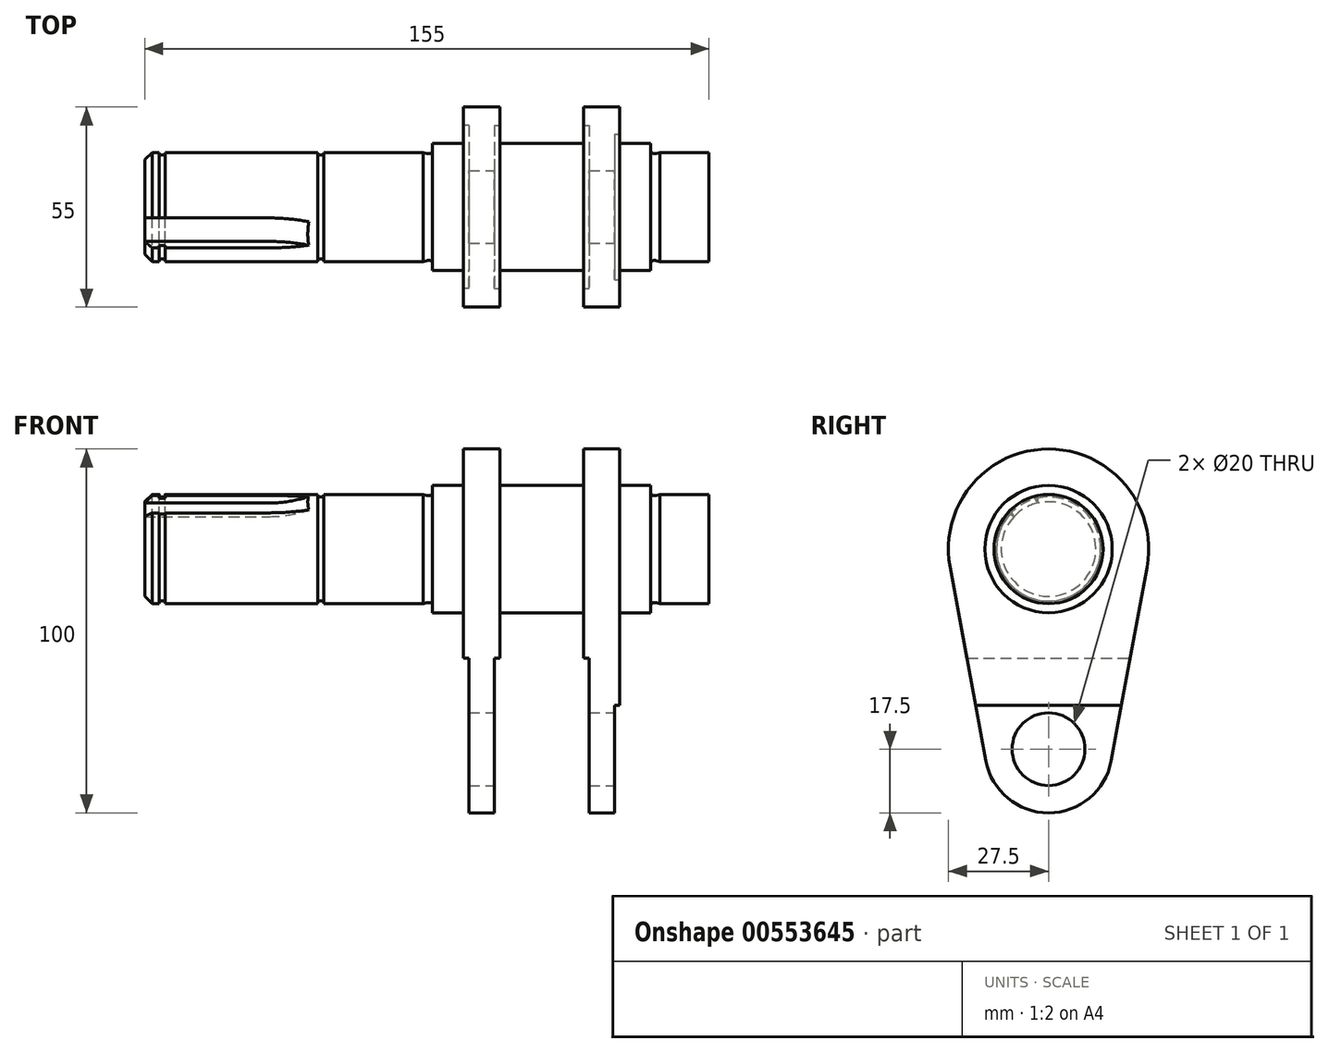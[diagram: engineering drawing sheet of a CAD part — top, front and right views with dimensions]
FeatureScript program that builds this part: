
annotation { "Feature Type Name" : "Feature", "Feature Type Description" : "" }
export const myFeature = defineFeature(function(context is Context, id is Id, definition is map)
    precondition{}
    {
        {
            var Q0;
            Q0=qCreatedBy(makeId("Front.planeOp"),FACE);
            var sketch = newSketch(context, id + "F0", { "sketchPlane" : qUnion([Q0])});
            skLineSegment(sketch, "E0", {"start": v(-79, 0) * mm, "end": v(-79, 15) * mm});
            skLineSegment(sketch, "E1", {"start": v(-79, 15) * mm, "end": v(-75, 15) * mm});
            skLineSegment(sketch, "E2", {"start": v(0, 15.5) * mm, "end": v(0, 17.5) * mm});
            skLineSegment(sketch, "E3", {"start": v(0, 17.5) * mm, "end": v(60, 17.5) * mm});
            skLineSegment(sketch, "E4", {"start": v(60, 17.5) * mm, "end": v(60, 15.5) * mm});
            skLineSegment(sketch, "E5", {"start": v(62.5, 15) * mm, "end": v(76, 15) * mm});
            skLineSegment(sketch, "E6", {"start": v(76, 15) * mm, "end": v(76, 0) * mm});
            skLineSegment(sketch, "E7", {"start": v(76, 0) * mm, "end": v(-79, 0) * mm});
            skLineSegment(sketch, "E8", {"start": v(-2.5, 15) * mm, "end": v(-1.48, 14.73) * mm});
            skLineSegment(sketch, "E9", {"start": v(-1.28, 14.7) * mm, "end": v(-0.8, 14.7) * mm});
            skPoint(sketch, "E10.orphan", {"position": v(0, 15) * mm});
            skPoint(sketch, "E11.visualSharp", {"position": v(0, 14.7) * mm});
            skArc(sketch, "E11.filletArc", {"start": v(-0.8, 14.7) * mm, "mid": v(-0.23, 14.93) * mm, "end": v(0, 15.5) * mm});
            skPoint(sketch, "E12.visualSharp", {"position": v(-1.38, 14.7) * mm});
            skArc(sketch, "E12.filletArc", {"start": v(-1.48, 14.73) * mm, "mid": v(-1.38, 14.7) * mm, "end": v(-1.28, 14.7) * mm});
            skLineSegment(sketch, "E13", {"start": v(62.5, 15) * mm, "end": v(61.48, 14.73) * mm});
            skLineSegment(sketch, "E14", {"start": v(61.28, 14.7) * mm, "end": v(60.8, 14.7) * mm});
            skPoint(sketch, "E15.orphan", {"position": v(60, 15) * mm});
            skPoint(sketch, "E16.visualSharp", {"position": v(60, 14.7) * mm});
            skArc(sketch, "E16.filletArc", {"start": v(60, 15.5) * mm, "mid": v(60.23, 14.93) * mm, "end": v(60.8, 14.7) * mm});
            skPoint(sketch, "E17.visualSharp", {"position": v(61.38, 14.7) * mm});
            skArc(sketch, "E17.filletArc", {"start": v(61.28, 14.7) * mm, "mid": v(61.38, 14.7) * mm, "end": v(61.48, 14.73) * mm});
            skLineSegment(sketch, "E18", {"start": v(-75, 15) * mm, "end": v(-75, 14.3) * mm});
            skLineSegment(sketch, "E19", {"start": v(-75, 14.3) * mm, "end": v(-73.4, 14.3) * mm});
            skLineSegment(sketch, "E20", {"start": v(-73.4, 14.3) * mm, "end": v(-73.4, 15) * mm});
            skLineSegment(sketch, "E21", {"start": v(-31.5, 15) * mm, "end": v(-31.5, 14.3) * mm});
            skLineSegment(sketch, "E22", {"start": v(-31.5, 14.3) * mm, "end": v(-29.9, 14.3) * mm});
            skLineSegment(sketch, "E23", {"start": v(-29.9, 14.3) * mm, "end": v(-29.9, 15) * mm});
            skLineSegment(sketch, "E24.trimOffspring", {"start": v(-29.9, 15) * mm, "end": v(-2.5, 15) * mm});
            skLineSegment(sketch, "E25.trimOffspring", {"start": v(-73.4, 15) * mm, "end": v(-31.5, 15) * mm});
            skSolve(sketch);
        }
        {
            var Q0;
            Q0=makeQuery(id+"F0.imprint","IMPRINT",FACE,{"disambiguationData":[TD([[makeQuery(id+"F0.imprint","IMPRINT",EDGE,{"derivedFrom":sQuery(id+"F0.wireOp",EDGE,"E0")}),-1.0]])]});
            var Q1;
            Q1=sQuery(id+"F0.wireOp",EDGE,"E7");
            revolve(context, id + "F1", {"entities" : qUnion([Q0]), "axis" : qUnion([Q1]), "revolveType" : RevolveType.FULL});
        }
        {
            var Q0;
            Q0=makeQuery(id+"F1.opRevolve","SWEPT_EDGE",EDGE,{"disambiguationData":[OSD([sQuery(id+"F0.wireOp",EDGE,"E0"),sQuery(id+"F0.wireOp",EDGE,"E1")])]});
            chamfer(context, id + "F2", {"entities" : qUnion([Q0]), "width" : 2 * mm, "tangentPropagation" : true});
        }
        {
            var Q0;
            Q0=makeQuery(id+"F1.opRevolve","SWEPT_FACE",FACE,{"disambiguationData":[OSD([sQuery(id+"F0.wireOp",EDGE,"E0")])]});
            var sketch = newSketch(context, id + "F3", { "sketchPlane" : qUnion([Q0])});
            skArc(sketch, "E26", {"start": v(9.45, 8.92) * mm, "mid": v(6.5, 11.26) * mm, "end": v(3, 12.65) * mm});
            skLineSegment(sketch, "E27", {"start": v(3, 12.65) * mm, "end": v(3, 14.7) * mm});
            skLineSegment(sketch, "E28", {"start": v(0, 0) * mm, "end": v(11.26, 6.5) * mm, "construction": true});
            skLineSegment(sketch, "E29", {"start": v(9.45, 8.92) * mm, "end": v(11.23, 9.95) * mm});
            skArc(sketch, "E30", {"start": v(11.23, 9.95) * mm, "mid": v(7.5, 13) * mm, "end": v(3, 14.7) * mm});
            skLineSegment(sketch, "E31", {"start": v(6.5, 11.26) * mm, "end": v(0, 0) * mm, "construction": true});
            skSolve(sketch);
        }
        {
            var Q0;
            Q0=sQuery(id+"F3.wireOp",EDGE,"E26");
            cPoint(context, id + "F4", {"entities" : qUnion([Q0]), "parameter" : 0.5});
        }
        {
            var Q0;
            Q0=sQuery(id+"F3.wireOp",VERTEX,"E26.center");
            var Q1;
            Q1 = qCreatedBy(id + "F4" ,VERTEX);
            var Q2;
            Q2=qCreatedBy(makeId("Origin.pointOp"),VERTEX);
            cPlane(context, id + "F5", {"entities" : qUnion([Q0, Q1, Q2]), "cplaneType" : CPlaneType.THREE_POINT, "offset" : 25 * mm, "oppositeDirection" : true, "width" : 150 * mm, "height" : 150 * mm});
        }
        {
            var Q0;
            Q0=qCreatedBy(id+"F5.planeOp",FACE);
            var sketch = newSketch(context, id + "F6", { "sketchPlane" : qUnion([Q0])});
            skLineSegment(sketch, "E32", {"start": v(-79, 13) * mm, "end": v(-45, 13) * mm});
            skArc(sketch, "E33", {"start": v(-45, 13) * mm, "mid": v(-28.57, 17.9) * mm, "end": v(-17.5, 31) * mm});
            skSolve(sketch);
        }
        {
            var Q0;
            Q0 = qSketchRegion(id + "F3", true);
            var Q1;
            Q1 = qConstructionFilter(qBodyType(qCreatedBy(id + "F6" ,EDGE), BodyType.WIRE), ConstructionObject.NO);
            sweep(context, id + "F7", {"profiles" : qUnion([Q0]), "path" : qUnion([Q1])});
        }
        {
            var Q0;
            Q0=makeQuery(id+"F7.opSweep","SWEPT_BODY",BODY,{"disambiguationData":[OSD([sQuery(id+"F3.wireOp",EDGE,"E26"),sQuery(id+"F3.wireOp",EDGE,"E27"),sQuery(id+"F3.wireOp",EDGE,"E29"),sQuery(id+"F3.wireOp",EDGE,"E30"),sQuery(id+"F6.wireOp",EDGE,"E33")])]});
            var Q1;
            Q1=makeQuery(id+"FzIJVg3da7VtIe4_2.1.F7.opSweep","SWEPT_BODY",BODY,{"disambiguationData":[OSD([sQuery(id+"F3.wireOp",EDGE,"E26"),sQuery(id+"F3.wireOp",EDGE,"E27"),sQuery(id+"F3.wireOp",EDGE,"E29"),sQuery(id+"F3.wireOp",EDGE,"E30"),sQuery(id+"F6.wireOp",EDGE,"E33")])]});
            var Q2;
            Q2=makeQuery(id+"FzIJVg3da7VtIe4_2.2.F7.opSweep","SWEPT_BODY",BODY,{"disambiguationData":[OSD([sQuery(id+"F3.wireOp",EDGE,"E26"),sQuery(id+"F3.wireOp",EDGE,"E27"),sQuery(id+"F3.wireOp",EDGE,"E29"),sQuery(id+"F3.wireOp",EDGE,"E30"),sQuery(id+"F6.wireOp",EDGE,"E33")])]});
            var Q3;
            Q3=makeQuery(id+"FzIJVg3da7VtIe4_2.3.F7.opSweep","SWEPT_BODY",BODY,{"disambiguationData":[OSD([sQuery(id+"F3.wireOp",EDGE,"E26"),sQuery(id+"F3.wireOp",EDGE,"E27"),sQuery(id+"F3.wireOp",EDGE,"E29"),sQuery(id+"F3.wireOp",EDGE,"E30"),sQuery(id+"F6.wireOp",EDGE,"E33")])]});
            var Q4;
            Q4=makeQuery(id+"FzIJVg3da7VtIe4_2.4.F7.opSweep","SWEPT_BODY",BODY,{"disambiguationData":[OSD([sQuery(id+"F3.wireOp",EDGE,"E26"),sQuery(id+"F3.wireOp",EDGE,"E27"),sQuery(id+"F3.wireOp",EDGE,"E29"),sQuery(id+"F3.wireOp",EDGE,"E30"),sQuery(id+"F6.wireOp",EDGE,"E33")])]});
            var Q5;
            Q5=makeQuery(id+"FzIJVg3da7VtIe4_2.5.F7.opSweep","SWEPT_BODY",BODY,{"disambiguationData":[OSD([sQuery(id+"F3.wireOp",EDGE,"E26"),sQuery(id+"F3.wireOp",EDGE,"E27"),sQuery(id+"F3.wireOp",EDGE,"E29"),sQuery(id+"F3.wireOp",EDGE,"E30"),sQuery(id+"F6.wireOp",EDGE,"E33")])]});
            var Q6;
            Q6=makeQuery(id+"F1.opRevolve","SWEPT_BODY",BODY,{"disambiguationData":[OSD([sQuery(id+"F0.wireOp",EDGE,"E0"),sQuery(id+"F0.wireOp",EDGE,"E1"),sQuery(id+"F0.wireOp",EDGE,"E2"),sQuery(id+"F0.wireOp",EDGE,"E3"),sQuery(id+"F0.wireOp",EDGE,"E4"),sQuery(id+"F0.wireOp",EDGE,"E5"),sQuery(id+"F0.wireOp",EDGE,"E6"),sQuery(id+"F0.wireOp",EDGE,"E7"),sQuery(id+"F0.wireOp",EDGE,"E8"),sQuery(id+"F0.wireOp",EDGE,"E9"),sQuery(id+"F0.wireOp",EDGE,"E11.filletArc"),sQuery(id+"F0.wireOp",EDGE,"E12.filletArc"),sQuery(id+"F0.wireOp",EDGE,"E13"),sQuery(id+"F0.wireOp",EDGE,"E14"),sQuery(id+"F0.wireOp",EDGE,"E16.filletArc"),sQuery(id+"F0.wireOp",EDGE,"E17.filletArc"),sQuery(id+"F0.wireOp",EDGE,"E18"),sQuery(id+"F0.wireOp",EDGE,"E19"),sQuery(id+"F0.wireOp",EDGE,"E20"),sQuery(id+"F0.wireOp",EDGE,"E21"),sQuery(id+"F0.wireOp",EDGE,"E22"),sQuery(id+"F0.wireOp",EDGE,"E23"),sQuery(id+"F0.wireOp",EDGE,"E24.trimOffspring"),sQuery(id+"F0.wireOp",EDGE,"E25.trimOffspring")])]});
            booleanBodies(context, id + "F8", {"operationType" : BooleanOperationType.SUBTRACTION, "tools" : qUnion([Q0, Q1, Q2, Q3, Q4, Q5]), "targets" : qUnion([Q6])});
        }
        {
            var Q0;
            Q0=makeQuery(id+"F1.opRevolve","SWEPT_FACE",FACE,{"disambiguationData":[OSD([sQuery(id+"F0.wireOp",EDGE,"E6")])]});
            var sketch = newSketch(context, id + "F9", { "sketchPlane" : qUnion([Q0])});
            skArc(sketch, "E34", {"start": v(27.04, -5) * mm, "mid": v(0, 27.5) * mm, "end": v(-27.04, -5) * mm});
            skArc(sketch, "E35", {"start": v(-17.2, -58.18) * mm, "mid": v(0, -72.5) * mm, "end": v(17.2, -58.18) * mm});
            skLineSegment(sketch, "E36", {"start": v(-27.04, -5) * mm, "end": v(-17.2, -58.18) * mm});
            skLineSegment(sketch, "E37", {"start": v(27.04, -5) * mm, "end": v(17.2, -58.18) * mm});
            skCircle(sketch, "E38", {"center": v(0, -55) * mm, "radius": 10 * mm});
            skSolve(sketch);
        }
        {
            var Q0;
            Q0=makeQuery(id+"F9.imprint","IMPRINT",FACE,{"disambiguationData":[TD([[makeQuery(id+"F9.imprint","IMPRINT",EDGE,{"derivedFrom":sQuery(id+"F9.wireOp",EDGE,"E34")}),1.0]])]});
            extrude(context, id + "F10", {"entities" : qUnion([Q0]), "operationType" : NewBodyOperationType.ADD, "oppositeDirection" : true, "depth" : (24.5 + 10 + 23 + 10) * mm, "offsetDistance" : 25 * mm, "hasSecondDirection" : true, "secondDirectionOppositeDirection" : true, "secondDirectionDepth" : (24.5 + 10 + 23) * mm});
        }
        {
            var Q0;
            Q0=makeQuery(id+"F9.imprint","IMPRINT",FACE,{"disambiguationData":[TD([[makeQuery(id+"F9.imprint","IMPRINT",EDGE,{"derivedFrom":sQuery(id+"F9.wireOp",EDGE,"E34")}),1.0]])]});
            extrude(context, id + "F11", {"entities" : qUnion([Q0]), "operationType" : NewBodyOperationType.ADD, "oppositeDirection" : true, "depth" : (24.5 + 10) * mm, "offsetDistance" : 25 * mm, "hasSecondDirection" : true, "secondDirectionOppositeDirection" : true, "secondDirectionDepth" : 24.5 * mm});
        }
        {
            var Q0;
            Q0=qCreatedBy(makeId("Front.planeOp"),FACE);
            var sketch = newSketch(context, id + "F12", { "sketchPlane" : qUnion([Q0])});
            skLineSegment(sketch, "E39.bottom", {"start": v(17, -30) * mm, "end": v(43, -30) * mm});
            skLineSegment(sketch, "E39.top", {"start": v(17, -78) * mm, "end": v(43, -78) * mm});
            skLineSegment(sketch, "E39.left", {"start": v(17, -30) * mm, "end": v(17, -78) * mm});
            skLineSegment(sketch, "E39.right", {"start": v(43, -30) * mm, "end": v(43, -78) * mm});
            skLineSegment(sketch, "E40.bottom", {"start": v(50, -43) * mm, "end": v(55, -43) * mm});
            skLineSegment(sketch, "E40.top", {"start": v(50, -78) * mm, "end": v(55, -78) * mm});
            skLineSegment(sketch, "E40.left", {"start": v(50, -43) * mm, "end": v(50, -78) * mm});
            skLineSegment(sketch, "E40.right", {"start": v(55, -43) * mm, "end": v(55, -78) * mm});
            skLineSegment(sketch, "E41.bottom", {"start": v(10, -30) * mm, "end": v(5, -30) * mm});
            skLineSegment(sketch, "E41.top", {"start": v(10, -78) * mm, "end": v(5, -78) * mm});
            skLineSegment(sketch, "E41.left", {"start": v(10, -30) * mm, "end": v(10, -78) * mm});
            skLineSegment(sketch, "E41.right", {"start": v(5, -30) * mm, "end": v(5, -78) * mm});
            skSolve(sketch);
        }
        {
            var Q0;
            Q0 = qSketchRegion(id + "F12", true);
            extrude(context, id + "F13", {"entities" : qUnion([Q0]), "operationType" : NewBodyOperationType.REMOVE, "endBound" : BoundingType.THROUGH_ALL, "oppositeDirection" : true, "depth" : 25 * mm, "offsetDistance" : 25 * mm, "hasSecondDirection" : true, "secondDirectionBound" : SecondDirectionBoundingType.THROUGH_ALL, "secondDirectionOppositeDirection" : false, "secondDirectionDepth" : 25 * mm});
        }
    });
